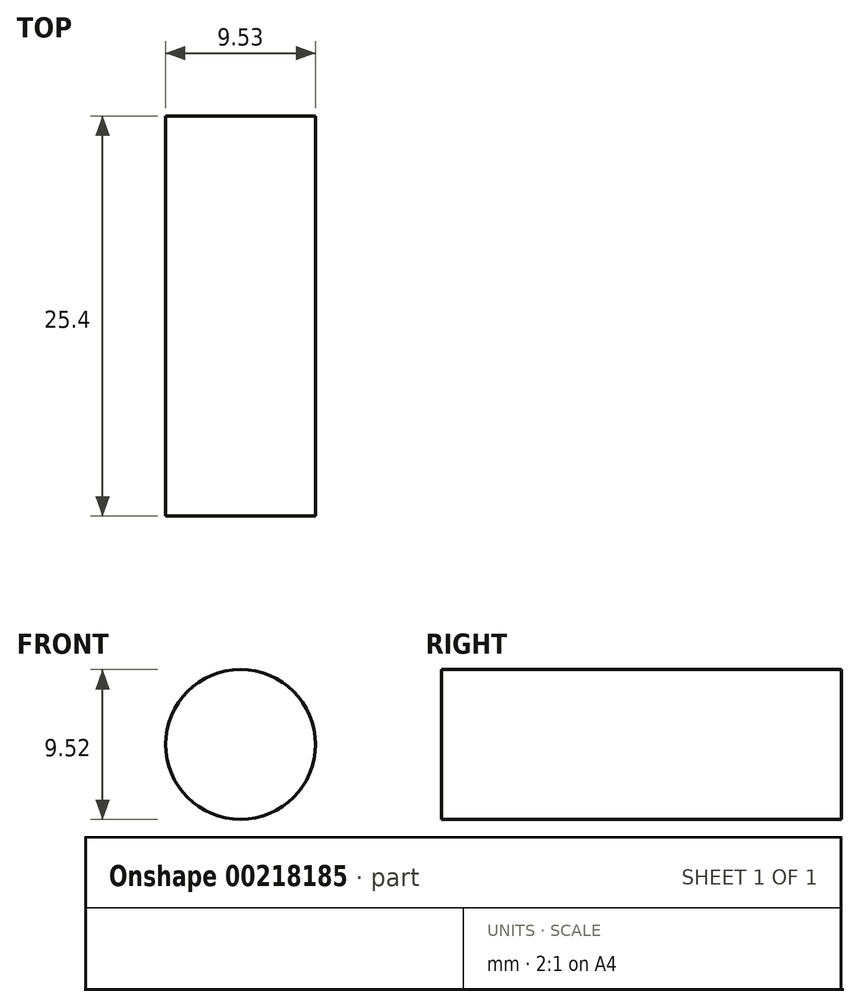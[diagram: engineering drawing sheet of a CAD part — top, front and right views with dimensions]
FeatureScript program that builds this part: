
annotation { "Feature Type Name" : "Feature", "Feature Type Description" : "" }
export const myFeature = defineFeature(function(context is Context, id is Id, definition is map)
    precondition{}
    {
        {
            var Q0;
            Q0=qCreatedBy(makeId("Top.planeOp"),FACE);
            var sketch = newSketch(context, id + "F0", { "sketchPlane" : qUnion([Q0])});
            skLineSegment(sketch, "E0.bottom", {"start": v(-38.1, 25.4) * mm, "end": v(38.1, 25.4) * mm});
            skLineSegment(sketch, "E0.top", {"start": v(-38.1, -25.4) * mm, "end": v(38.1, -25.4) * mm});
            skLineSegment(sketch, "E0.left", {"start": v(-38.1, 25.4) * mm, "end": v(-38.1, -25.4) * mm});
            skLineSegment(sketch, "E0.right", {"start": v(38.1, 25.4) * mm, "end": v(38.1, -25.4) * mm});
            skLineSegment(sketch, "E1", {"start": v(0, 25.4) * mm, "end": v(0, -25.4) * mm, "construction": true});
            skLineSegment(sketch, "E2", {"start": v(38.1, 0) * mm, "end": v(-38.1, 0) * mm, "construction": true});
            skSolve(sketch);
        }
        {
            var Q0;
            Q0=makeQuery(id+"F0.imprint","IMPRINT",FACE,{"disambiguationData":[TD([[makeQuery(id+"F0.imprint","IMPRINT",EDGE,{"derivedFrom":sQuery(id+"F0.wireOp",EDGE,"E0.bottom")}),-1.0]])]});
            extrude(context, id + "F1", {"entities" : qUnion([Q0]), "endBound" : BoundingType.SYMMETRIC, "depth" : 25.4 * mm});
        }
        {
            var Q0;
            Q0=makeQuery(id+"F1.opExtrude","CAP_FACE",FACE,{"disambiguationData":[OSD([sQuery(id+"F0.wireOp",EDGE,"E0.bottom"),sQuery(id+"F0.wireOp",EDGE,"E0.top"),sQuery(id+"F0.wireOp",EDGE,"E0.left"),sQuery(id+"F0.wireOp",EDGE,"E0.right")])],"isStart":false});
            var sketch = newSketch(context, id + "F2", { "sketchPlane" : qUnion([Q0])});
            skLineSegment(sketch, "E3.bottom", {"start": v(-20, 0.39) * mm, "end": v(20, 0.39) * mm});
            skLineSegment(sketch, "E3.top", {"start": v(-20, -0.4) * mm, "end": v(20, -0.4) * mm});
            skLineSegment(sketch, "E3.left", {"start": v(-20, 0.39) * mm, "end": v(-20, -0.4) * mm});
            skLineSegment(sketch, "E3.right", {"start": v(20, 0.39) * mm, "end": v(20, -0.4) * mm});
            skLineSegment(sketch, "E4", {"start": v(0, 0.4) * mm, "end": v(0, -0.4) * mm, "construction": true});
            skLineSegment(sketch, "E5", {"start": v(-20, 0) * mm, "end": v(20, 0) * mm, "construction": true});
            skLineSegment(sketch, "E6.bottom", {"start": v(-38.1, 25.4) * mm, "end": v(38.1, 25.4) * mm});
            skLineSegment(sketch, "E6.top", {"start": v(-38.1, 0) * mm, "end": v(38.1, 0) * mm});
            skLineSegment(sketch, "E6.left", {"start": v(-38.1, 25.4) * mm, "end": v(-38.1, 0) * mm});
            skLineSegment(sketch, "E6.right", {"start": v(38.1, 25.4) * mm, "end": v(38.1, 0) * mm});
            skSolve(sketch);
        }
        {
            var Q0;
            {var subQ1=sQuery(id+"F2.wireOp",EDGE,"E3.bottom");Q0=makeQuery(id+"F2.imprint","IMPRINT",FACE,{"disambiguationData":[TD([[makeQuery(id+"F2.imprint","IMPRINT",EDGE,{"derivedFrom":subQ1}),1.0]])]});}
            var Q1;
            {var subQ0=sQuery(id+"F2.wireOp",EDGE,"E3.bottom");Q1=makeQuery(id+"F2.imprint","IMPRINT",FACE,{"disambiguationData":[TD([[makeQuery(id+"F2.imprint","IMPRINT",EDGE,{"derivedFrom":subQ0}),-1.0]])]});}
            var Q2;
            {var subQ0=sQuery(id+"F2.wireOp",EDGE,"E3.top");Q2=makeQuery(id+"F2.imprint","IMPRINT",FACE,{"disambiguationData":[TD([[makeQuery(id+"F2.imprint","IMPRINT",EDGE,{"derivedFrom":subQ0}),1.0]])]});}
            extrude(context, id + "F3", {"entities" : qUnion([Q0, Q1, Q2]), "operationType" : NewBodyOperationType.REMOVE, "oppositeDirection" : true, "depth" : 25.4 * mm});
        }
        {
            var Q0;
            Q0=makeQuery(id+"F1.opExtrude","SWEPT_FACE",FACE,{"disambiguationData":[OSD([sQuery(id+"F0.wireOp",EDGE,"E0.top")])]});
            var sketch = newSketch(context, id + "F4", { "sketchPlane" : qUnion([Q0])});
            skCircle(sketch, "E7", {"center": v(-28.58, 0) * mm, "radius": 4.76 * mm});
            skCircle(sketch, "E8.MirrorC", {"center": v(28.58, 0) * mm, "radius": 4.76 * mm});
            skSolve(sketch);
        }
        {
            var Q0;
            Q0=makeQuery(id+"F4.imprint","IMPRINT",FACE,{"disambiguationData":[TD([[makeQuery(id+"F4.imprint","IMPRINT",EDGE,{"derivedFrom":sQuery(id+"F4.wireOp",EDGE,"E7")}),1.0]])]});
            var Q1;
            Q1=makeQuery(id+"F4.imprint","IMPRINT",FACE,{"disambiguationData":[TD([[makeQuery(id+"F4.imprint","IMPRINT",EDGE,{"derivedFrom":sQuery(id+"F4.wireOp",EDGE,"E8.MirrorC")}),-1.0]])]});
            extrude(context, id + "F5", {"entities" : qUnion([Q0, Q1]), "operationType" : NewBodyOperationType.REMOVE, "oppositeDirection" : true, "depth" : 25.4 * mm});
        }
    });
